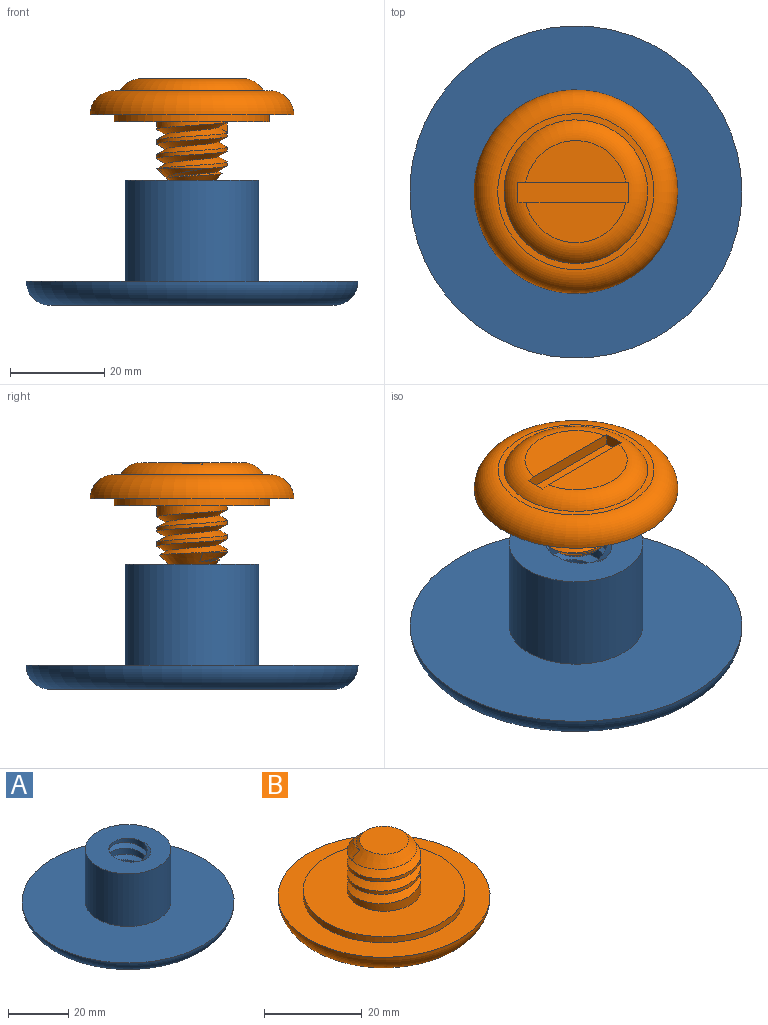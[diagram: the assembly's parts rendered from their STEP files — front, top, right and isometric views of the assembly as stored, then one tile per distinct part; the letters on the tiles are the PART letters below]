
ASSEMBLY  parts=2 mates=1
PART A: 10 faces, bbox 77.1x77.1x28.7 mm
  f0: cylinder r=6.41mm len=21.43mm, axis (0,0,-1), area 465mm2, adj f1,f3,f4,f5,f8
  f1: plane 29.15x29.15mm, normal (0,0,1), area 485.3mm2, adj f0,f2,f4,f5
  f2: cylinder r=14.22mm len=28.45mm, axis (0,0,-1), area 1915.4mm2, adj f1,f7
  f3: plane 2.29x1.98mm, normal (0,-1,0), area 2.3mm2, adj f0,f4,f5
  f4: bspline ~23.37x19.38mm, area 466.6mm2, adj f0,f1,f3,f5
  f5: bspline ~22.57x19.38mm, area 442.5mm2, adj f0,f1,f3,f4
  f6: plane 60.4x60.4mm, normal (0,0,-1), area 2865.2mm2, adj f9
  f7: plane 70.56x70.56mm, normal (0,0,1), area 3274.6mm2, adj f2,f9
  f8: plane 12.83x12.83mm, normal (0,0,1), area 129.2mm2, adj f0
  f9: torus R=30.2mm, axis (0,0,1), area 1676.3mm2, adj f6,f7
PART B: 20 faces, bbox 46.9x46.9x22.3 mm
  f0: cylinder r=7.51mm len=15.03mm, axis (0,0,-1), area 164.3mm2, adj f13,f15,f17,f18,f19
  f1: plane 21.33x8.85mm, normal (0,0,-1), area 141.7mm2, adj f7,f10
  f2: plane 43.3x43.3mm, normal (0,0,1), area 616.8mm2, adj f11,f12
  f3: plane 33.14x33.14mm, normal (0,0,-1), area 131.6mm2, adj f10,f11
  f4: plane 4.26x2.33mm, normal (1,0,0), area 9.9mm2, adj f5,f7,f9,f10
  f5: plane 23.6x2.57mm, normal (0,-1,0), area 59.7mm2, adj f4,f6,f8,f9,f10
  f6: plane 4.26x2.52mm, normal (-1,0,0), area 10.7mm2, adj f5,f7,f9,f10
  f7: plane 23.6x2.56mm, normal (0,1,0), area 59.7mm2, adj f1,f4,f6,f9,f10
  f8: plane 21.23x8.6mm, normal (0,0,-1), area 136.4mm2, adj f5,f10
  f9: plane 23.58x4.26mm, normal (0,0,-1), area 100.5mm2, adj f4,f5,f6,f7
  f10: torus R=10.85mm, axis (0,0,-1), area 435.1mm2, adj f1,f3,f4,f5,f6,f7,f8
  f11: torus R=16.57mm, axis (0,0,1), area 992.9mm2, adj f2,f3
  f12: cylinder r=16.5mm len=33.01mm, axis (0,0,-1), area 158mm2, adj f2,f13
  f13: plane 33.01x33.01mm, normal (0,0,1), area 678.2mm2, adj f0,f12
  f14: plane 9.95x9.95mm, normal (0,0,1), area 77.7mm2, adj f16
  f15: cone r=4.97mm half-angle=45deg, axis (0,0,-1), area 16mm2, adj f0,f16,f18,f19
  f16: cone r=4.97mm half-angle=45deg, axis (0,0,-1), area 80.6mm2, adj f14,f15,f19
  f17: plane 2.29x1.98mm, normal (0,1,0), area 2.3mm2, adj f0,f18,f19
  f18: bspline ~17.35x15.03mm, area 310.8mm2, adj f0,f15,f17,f19
  f19: bspline ~17.35x15.03mm, area 274.9mm2, adj f0,f15,f16,f17,f18
PLACE A rot(axis=(1,0,0),0deg) t=(7.37,8.15,10.11)mm
PLACE B rot(axis=(-1,0,0),180deg) t=(7.37,62.5,75.61)mm
MATE slider B.f0 <-> A.f0  axis (0,0,-1) through (7.37,8.15,31.54)mm
